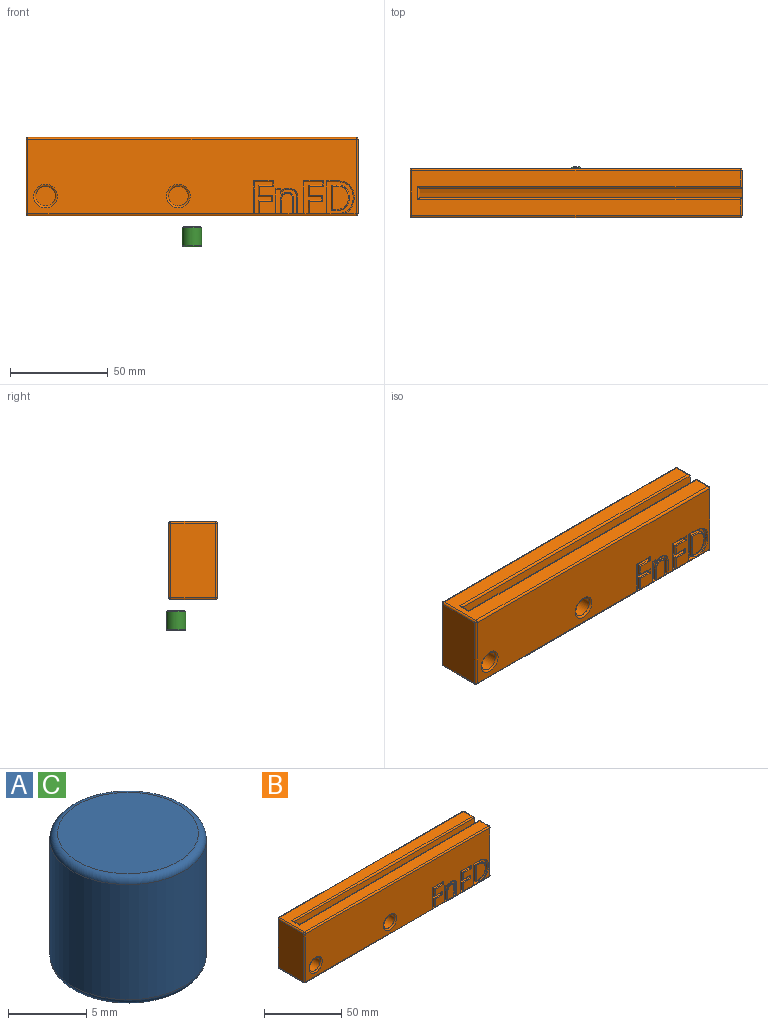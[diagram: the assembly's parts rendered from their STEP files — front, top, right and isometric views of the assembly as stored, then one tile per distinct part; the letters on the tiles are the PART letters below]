
ASSEMBLY  parts=3 mates=1
PART A: 5 faces, bbox 10.8x10.8x10 mm
  f0: cylinder r=5mm len=10mm, axis (0,0,-1), area 282.7mm2, adj f3,f4
  f1: plane 9x9mm, normal (0,0,1), area 63.6mm2, adj f4
  f2: plane 9x9mm, normal (0,0,-1), area 63.6mm2, adj f3
  f3: torus R=4.5mm, axis (0,0,1), area 23.8mm2, adj f0,f2
  f4: torus R=4.5mm, axis (0,0,1), area 23.8mm2, adj f0,f1
PART B: 249 faces, bbox 170.1x25.1x40.1 mm
  f0: plane 168x38.01mm, normal (0,-1,0), area 5632.2mm2, adj f21,f22,f24,f25,f27,f28,f165,f166
  f1: plane 10.36x5.51mm, normal (0,-1,0), area 54.3mm2, adj f27,f159,f160,f161,f162,f163,f164
  f2: plane 168x38.01mm, normal (0,1,0), area 5632.2mm2, adj f19,f20,f35,f36,f42,f43,f204,f205
  f3: plane 168x23mm, normal (0,0,1), area 2730.5mm2, adj f24,f33,f34,f38,f41,f42,f44,f46
  f4: plane 38x23mm, normal (-1,0,0), area 874mm2, adj f25,f26,f34,f35
  f5: plane 168x23mm, normal (0,0,-1), area 3864mm2, adj f26,f27,f36,f37
  f6: plane 38x23mm, normal (1,0,0), area 786.4mm2, adj f8,f9,f28,f33,f37,f43,f46
  f7: plane 10.36x5.51mm, normal (0,1,0), area 54.3mm2, adj f36,f213,f214,f215,f216,f217,f218
  f8: plane 165x36.07mm, normal (0,1,0.07), area 5964.7mm2, adj f6,f9,f10,f33,f38,f41
  f9: plane 165x36.07mm, normal (0,-1,0.07), area 5964.7mm2, adj f6,f8,f10,f41,f44,f46
  f10: plane 36x4.87mm, normal (1,0,0), area 87.6mm2, adj f8,f9,f41
  f11: cylinder r=5.05mm len=10.1mm, axis (0,-1,0), area 288.7mm2, adj f12,f21
  f12: plane 10.1x10.1mm, normal (0,-1,0), area 80.1mm2, adj f11
  f13: cylinder r=5.05mm len=10.1mm, axis (0,-1,0), area 288.7mm2, adj f14,f22
  f14: plane 10.1x10.1mm, normal (0,-1,0), area 80.1mm2, adj f13
  f15: cylinder r=5.05mm len=10.1mm, axis (0,1,0), area 288.7mm2, adj f16,f19
  f16: plane 10.1x10.1mm, normal (0,1,0), area 80.1mm2, adj f15
  f17: cylinder r=5.05mm len=10.1mm, axis (0,1,0), area 288.7mm2, adj f18,f20
  f18: plane 10.1x10.1mm, normal (0,1,0), area 80.1mm2, adj f17
  f19: torus R=6.05mm, axis (0,-1,0), area 53.4mm2, adj f2,f15
  f20: torus R=6.05mm, axis (0,-1,0), area 53.4mm2, adj f2,f17
  f21: torus R=6.05mm, axis (0,-1,0), area 53.4mm2, adj f0,f11
  f22: torus R=6.05mm, axis (0,-1,0), area 53.4mm2, adj f0,f13
  f23: sphere r=1mm, area 1.6mm2, adj f25,f26,f27
  f24: cylinder r=1mm len=168mm, axis (1,0,0), area 263.9mm2, adj f0,f3,f29,f30
  f25: cylinder r=1mm len=38mm, axis (0,0,1), area 59.7mm2, adj f0,f4,f23,f30
  f26: cylinder r=1mm len=23mm, axis (0,1,0), area 36.1mm2, adj f4,f5,f23,f31
  f27: cylinder r=1mm len=168mm, axis (-1,0,0), area 263.9mm2, adj f0,f1,f5,f23,f32,f112,f123,f130
  f28: cylinder r=1mm len=38mm, axis (0,0,-1), area 59.7mm2, adj f0,f6,f29,f32
  f29: sphere r=1mm, area 1.6mm2, adj f24,f28,f33
  f30: sphere r=1mm, area 1.6mm2, adj f24,f25,f34
  f31: sphere r=1mm, area 1.6mm2, adj f26,f35,f36
  f32: sphere r=1mm, area 1.6mm2, adj f27,f28,f37
  f33: cylinder r=1mm len=9.07mm, axis (0,1,0), area 13.7mm2, adj f3,f6,f8,f29,f38
  f34: cylinder r=1mm len=23mm, axis (0,-1,0), area 36.1mm2, adj f3,f4,f30,f39
  f35: cylinder r=1mm len=38mm, axis (0,0,-1), area 59.7mm2, adj f2,f4,f31,f39
  f36: cylinder r=1mm len=168mm, axis (1,0,0), area 263.9mm2, adj f2,f5,f7,f31,f40,f56,f59,f83
  f37: cylinder r=1mm len=23mm, axis (0,-1,0), area 36.1mm2, adj f5,f6,f32,f40
  f38: cylinder r=1mm len=166mm, axis (-1,0,0), area 248mm2, adj f3,f8,f33,f41
  f39: sphere r=1mm, area 1mm2, adj f34,f35,f42
  f40: sphere r=1mm, area 1mm2, adj f36,f37,f43
  f41: cylinder r=1mm len=6.87mm, axis (0,1,0), area 8.8mm2, adj f3,f8,f9,f10,f38,f44
  f42: cylinder r=1mm len=168mm, axis (-1,0,0), area 263.9mm2, adj f2,f3,f39,f45
  f43: cylinder r=1mm len=38mm, axis (0,0,1), area 59.7mm2, adj f2,f6,f40,f45
  f44: cylinder r=1mm len=166mm, axis (-1,0,0), area 248mm2, adj f3,f9,f41,f46
  f45: sphere r=1mm, area 1.6mm2, adj f42,f43,f46
  f46: cylinder r=1mm len=9.07mm, axis (0,1,0), area 13.7mm2, adj f3,f6,f9,f44,f45
  f47: plane 6.96x1.5mm, normal (1,0,0), area 10.4mm2, adj f48,f56,f57,f247
  f48: plane 6.75x1.5mm, normal (0,0,1), area 10.1mm2, adj f47,f49,f57,f248
  f49: plane 1.68x1.5mm, normal (1,0,0), area 2.5mm2, adj f48,f50,f57,f246
  f50: plane 6.75x1.5mm, normal (0,0,-1), area 10.1mm2, adj f49,f51,f57,f245
  f51: plane 5.96x1.5mm, normal (1,0,0), area 8.9mm2, adj f50,f52,f57,f244
  f52: plane 7.19x1.5mm, normal (0,0,1), area 10.8mm2, adj f51,f53,f57,f243
  f53: plane 1.68x1.5mm, normal (1,0,0), area 2.5mm2, adj f52,f54,f57,f242
  f54: plane 9.08x1.5mm, normal (0,0,-1), area 13.6mm2, adj f53,f55,f57,f241
  f55: plane 16.29x1.5mm, normal (-1,0,0), area 24.4mm2, adj f54,f56,f57,f240
  f56: plane 2.89x2mm, normal (0,0,1), area 3.9mm2, adj f36,f47,f55,f57,f240,f247
  f57: plane 16.29x9.08mm, normal (0,1,0), area 54.3mm2, adj f47,f48,f49,f50,f51,f52,f53,f54
  f58: plane 16.29x1.5mm, normal (-1,0,0), area 24.4mm2, adj f59,f71,f72,f228
  f59: plane 8.74x2.12mm, normal (0,0,1), area 9.8mm2, adj f36,f58,f60,f72,f227,f228
  f60: extruded ~6.3x2.13mm, area 10.2mm2, adj f59,f61,f72,f227
  f61: extruded ~6.17x2.19mm, area 10.1mm2, adj f60,f62,f72,f229
  f62: extruded ~5.88x2.11mm, area 9.6mm2, adj f61,f63,f72,f231
  f63: extruded ~5.9x2.11mm, area 9.7mm2, adj f62,f71,f72,f232
  f64: extruded ~4.93x1.71mm, area 8mm2, adj f65,f70,f72,f237
  f65: extruded ~5.09x1.67mm, area 8.2mm2, adj f64,f66,f72,f235
  f66: plane 2.31x1.5mm, normal (0,0,-1), area 3.5mm2, adj f65,f67,f72,f233
  f67: plane 13.01x1.5mm, normal (1,0,0), area 19.5mm2, adj f66,f68,f72,f234
  f68: plane 2.75x1.5mm, normal (0,0,1), area 4.1mm2, adj f67,f69,f72,f236
  f69: extruded ~4.75x1.61mm, area 7.7mm2, adj f68,f70,f72,f238
  f70: extruded ~4.8x1.6mm, area 7.8mm2, adj f64,f69,f72,f239
  f71: plane 4.99x1.5mm, normal (0,0,-1), area 7.5mm2, adj f58,f63,f72,f230
  f72: plane 16.29x13mm, normal (0,1,0), area 83.9mm2, adj f58,f59,f60,f61,f62,f63,f64,f65
  f73: plane 12.01x8.1mm, normal (0,1,0), area 85.3mm2, adj f233,f234,f235,f236,f237,f238,f239
  f74: plane 7.96x1.5mm, normal (1,0,0), area 11.9mm2, adj f75,f90,f91,f225
  f75: extruded ~3.41x1.5mm, area 5.5mm2, adj f74,f76,f91,f226
  f76: extruded ~3.32x1.5mm, area 5.4mm2, adj f75,f77,f91,f224
  f77: extruded ~2.28x1.5mm, area 3.5mm2, adj f76,f78,f91,f223
  f78: extruded ~1.6x1.5mm, area 3.2mm2, adj f77,f79,f91,f222
  f79: plane 1.71x0.1mm, normal (0,0,-1), area 0.1mm2, adj f78,f80,f91,f221,f222
  f80: plane 1.67x1.5mm, normal (0.98,0,-0.18), area 2.5mm2, adj f79,f81,f91,f221
  f81: plane 1.5x1.5mm, normal (0,0,-1), area 2.3mm2, adj f80,f82,f91,f220
  f82: plane 12.21x1.5mm, normal (-1,0,0), area 18.3mm2, adj f81,f83,f91,f219
  f83: plane 2.85x2mm, normal (0,0,1), area 3.8mm2, adj f36,f82,f84,f91,f213,f219
  f84: plane 6.41x1.5mm, normal (1,0,0), area 9.6mm2, adj f83,f85,f91,f213
  f85: extruded ~3.42x1.5mm, area 5.4mm2, adj f84,f86,f91,f214
  f86: extruded ~2.81x1.5mm, area 4.6mm2, adj f85,f87,f91,f215
  f87: extruded ~2.13x1.5mm, area 3.5mm2, adj f86,f88,f91,f217
  f88: extruded ~2.23x1.5mm, area 3.6mm2, adj f87,f89,f91,f218
  f89: plane 7.9x1.5mm, normal (-1,0,0), area 11.8mm2, adj f88,f90,f91,f216
  f90: plane 2.85x2mm, normal (0,0,1), area 3.8mm2, adj f36,f74,f89,f91,f216,f225
  f91: plane 12.43x10.21mm, normal (0,1,0), area 54mm2, adj f74,f75,f76,f77,f78,f79,f80,f81
  f92: plane 6.96x1.5mm, normal (1,0,0), area 10.4mm2, adj f93,f101,f102,f211
  f93: plane 6.75x1.5mm, normal (0,0,1), area 10.1mm2, adj f92,f94,f102,f212
  f94: plane 1.68x1.5mm, normal (1,0,0), area 2.5mm2, adj f93,f95,f102,f210
  f95: plane 6.75x1.5mm, normal (0,0,-1), area 10.1mm2, adj f94,f96,f102,f209
  f96: plane 5.96x1.5mm, normal (1,0,0), area 8.9mm2, adj f95,f97,f102,f208
  f97: plane 7.19x1.5mm, normal (0,0,1), area 10.8mm2, adj f96,f98,f102,f207
  f98: plane 1.68x1.5mm, normal (1,0,0), area 2.5mm2, adj f97,f99,f102,f206
  f99: plane 9.08x1.5mm, normal (0,0,-1), area 13.6mm2, adj f98,f100,f102,f205
  f100: plane 16.29x1.5mm, normal (-1,0,0), area 24.4mm2, adj f99,f101,f102,f204
  f101: plane 2.89x2mm, normal (0,0,1), area 3.9mm2, adj f36,f92,f100,f102,f204,f211
  f102: plane 16.29x9.08mm, normal (0,1,0), area 54.3mm2, adj f92,f93,f94,f95,f96,f97,f98,f99
  f103: plane 6.96x1.5mm, normal (-1,0,0), area 10.4mm2, adj f104,f112,f113,f172
  f104: plane 6.75x1.5mm, normal (0,0,1), area 10.1mm2, adj f103,f105,f113,f173
  f105: plane 1.68x1.5mm, normal (-1,0,0), area 2.5mm2, adj f104,f106,f113,f171
  f106: plane 6.75x1.5mm, normal (0,0,-1), area 10.1mm2, adj f105,f107,f113,f170
  f107: plane 5.96x1.5mm, normal (-1,0,0), area 8.9mm2, adj f106,f108,f113,f169
  f108: plane 7.19x1.5mm, normal (0,0,1), area 10.8mm2, adj f107,f109,f113,f168
  f109: plane 1.68x1.5mm, normal (-1,0,0), area 2.5mm2, adj f108,f110,f113,f167
  f110: plane 9.08x1.5mm, normal (0,0,-1), area 13.6mm2, adj f109,f111,f113,f166
  f111: plane 16.29x1.5mm, normal (1,0,0), area 24.4mm2, adj f110,f112,f113,f165
  f112: plane 2.89x2mm, normal (0,0,1), area 3.9mm2, adj f27,f103,f111,f113,f165,f172
  f113: plane 16.29x9.08mm, normal (0,-1,0), area 54.3mm2, adj f103,f104,f105,f106,f107,f108,f109,f110
  f114: plane 7.96x1.5mm, normal (-1,0,0), area 11.9mm2, adj f115,f130,f131,f180
  f115: extruded ~3.41x1.5mm, area 5.5mm2, adj f114,f116,f131,f181
  f116: extruded ~3.32x1.5mm, area 5.4mm2, adj f115,f117,f131,f179
  f117: extruded ~2.28x1.5mm, area 3.5mm2, adj f116,f118,f131,f178
  f118: extruded ~1.6x1.5mm, area 3.2mm2, adj f117,f119,f131,f177
  f119: plane 1.71x0.1mm, normal (0,0,-1), area 0.1mm2, adj f118,f120,f131,f176,f177
  f120: plane 1.67x1.5mm, normal (-0.98,0,-0.18), area 2.5mm2, adj f119,f121,f131,f176
  f121: plane 1.5x1.5mm, normal (0,0,-1), area 2.3mm2, adj f120,f122,f131,f175
  f122: plane 12.21x1.5mm, normal (1,0,0), area 18.3mm2, adj f121,f123,f131,f174
  f123: plane 2.85x2mm, normal (0,0,1), area 3.8mm2, adj f27,f122,f124,f131,f164,f174
  f124: plane 6.41x1.5mm, normal (-1,0,0), area 9.6mm2, adj f123,f125,f131,f164
  f125: extruded ~3.42x1.5mm, area 5.4mm2, adj f124,f126,f131,f163
  f126: extruded ~2.81x1.5mm, area 4.6mm2, adj f125,f127,f131,f162
  f127: extruded ~2.13x1.5mm, area 3.5mm2, adj f126,f128,f131,f161
  f128: extruded ~2.23x1.5mm, area 3.6mm2, adj f127,f129,f131,f160
  f129: plane 7.9x1.5mm, normal (1,0,0), area 11.8mm2, adj f128,f130,f131,f159
  f130: plane 2.85x2mm, normal (0,0,1), area 3.8mm2, adj f27,f114,f129,f131,f159,f180
  f131: plane 12.43x10.21mm, normal (0,-1,0), area 54mm2, adj f114,f115,f116,f117,f118,f119,f120,f121
  f132: plane 6.96x1.5mm, normal (-1,0,0), area 10.4mm2, adj f133,f141,f142,f182
  f133: plane 6.75x1.5mm, normal (0,0,1), area 10.1mm2, adj f132,f134,f142,f183
  f134: plane 1.68x1.5mm, normal (-1,0,0), area 2.5mm2, adj f133,f135,f142,f184
  f135: plane 6.75x1.5mm, normal (0,0,-1), area 10.1mm2, adj f134,f136,f142,f185
  f136: plane 5.96x1.5mm, normal (-1,0,0), area 8.9mm2, adj f135,f137,f142,f186
  f137: plane 7.19x1.5mm, normal (0,0,1), area 10.8mm2, adj f136,f138,f142,f187
  f138: plane 1.68x1.5mm, normal (-1,0,0), area 2.5mm2, adj f137,f139,f142,f188
  f139: plane 9.08x1.5mm, normal (0,0,-1), area 13.6mm2, adj f138,f140,f142,f189
  f140: plane 16.29x1.5mm, normal (1,0,0), area 24.4mm2, adj f139,f141,f142,f190
  f141: plane 2.89x2mm, normal (0,0,1), area 3.9mm2, adj f27,f132,f140,f142,f182,f190
  f142: plane 16.29x9.08mm, normal (0,-1,0), area 54.3mm2, adj f132,f133,f134,f135,f136,f137,f138,f139
  f143: plane 16.29x1.5mm, normal (1,0,0), area 24.4mm2, adj f144,f156,f157,f192
  f144: plane 8.74x2.12mm, normal (0,0,1), area 9.8mm2, adj f27,f143,f145,f157,f191,f192
  f145: extruded ~6.3x2.13mm, area 10.2mm2, adj f144,f146,f157,f191
  f146: extruded ~6.17x2.19mm, area 10.1mm2, adj f145,f147,f157,f193
  f147: extruded ~5.88x2.11mm, area 9.6mm2, adj f146,f148,f157,f195
  f148: extruded ~5.9x2.11mm, area 9.7mm2, adj f147,f156,f157,f196
  f149: extruded ~4.93x1.71mm, area 8mm2, adj f150,f155,f157,f202
  f150: extruded ~5.09x1.67mm, area 8.2mm2, adj f149,f151,f157,f203
  f151: plane 2.31x1.5mm, normal (0,0,-1), area 3.5mm2, adj f150,f152,f157,f201
  f152: plane 13.01x1.5mm, normal (-1,0,0), area 19.5mm2, adj f151,f153,f157,f199
  f153: plane 2.75x1.5mm, normal (0,0,1), area 4.1mm2, adj f152,f154,f157,f197
  f154: extruded ~4.75x1.61mm, area 7.7mm2, adj f153,f155,f157,f198
  f155: extruded ~4.8x1.6mm, area 7.8mm2, adj f149,f154,f157,f200
  f156: plane 4.99x1.5mm, normal (0,0,-1), area 7.5mm2, adj f143,f148,f157,f194
  f157: plane 16.29x13mm, normal (0,-1,0), area 83.9mm2, adj f143,f144,f145,f146,f147,f148,f149,f150
  f158: plane 12.01x8.1mm, normal (0,-1,0), area 85.3mm2, adj f197,f198,f199,f200,f201,f202,f203
  f159: cylinder r=0.5mm len=7.9mm, axis (0,0,1), area 6.2mm2, adj f1,f129,f130,f160
  f160: bspline ~3.42x1.34mm, area 1.8mm2, adj f1,f128,f159,f161
  f161: bspline ~3.1x1.34mm, area 1.7mm2, adj f1,f127,f160,f162
  f162: bspline ~3.37x1.72mm, area 2.3mm2, adj f1,f126,f161,f163
  f163: bspline ~5.58x1.78mm, area 2.7mm2, adj f1,f125,f162,f164
  f164: cylinder r=0.5mm len=6.41mm, axis (0,0,-1), area 5mm2, adj f1,f123,f124,f163
  f165: cylinder r=0.5mm len=16.79mm, axis (0,0,1), area 13mm2, adj f0,f111,f112,f166
  f166: cylinder r=0.5mm len=10.08mm, axis (1,0,0), area 7.5mm2, adj f0,f110,f165,f167
  f167: cylinder r=0.5mm len=2.68mm, axis (0,0,-1), area 1.7mm2, adj f0,f109,f166,f168
  f168: cylinder r=0.5mm len=7.69mm, axis (-1,0,0), area 5.6mm2, adj f0,f108,f167,f169
  f169: cylinder r=0.5mm len=5.96mm, axis (0,0,-1), area 4.3mm2, adj f0,f107,f168,f170
  f170: cylinder r=0.5mm len=7.25mm, axis (1,0,0), area 5.3mm2, adj f0,f106,f169,f171
  f171: cylinder r=0.5mm len=2.68mm, axis (0,0,-1), area 1.7mm2, adj f0,f105,f170,f173
  f172: cylinder r=0.5mm len=6.96mm, axis (0,0,-1), area 5.3mm2, adj f0,f103,f112,f173
  f173: cylinder r=0.5mm len=7.25mm, axis (-1,0,0), area 5.3mm2, adj f0,f104,f171,f172
  f174: cylinder r=0.5mm len=12.71mm, axis (0,0,1), area 9.8mm2, adj f0,f122,f123,f175
  f175: cylinder r=0.5mm len=2.42mm, axis (1,0,0), area 1.5mm2, adj f0,f121,f174,f176
  f176: cylinder r=0.5mm len=2.18mm, axis (0.18,0,-0.98), area 1.2mm2, adj f0,f119,f120,f175,f177
  f177: bspline ~2.45x2.41mm, area 1.5mm2, adj f0,f118,f119,f176,f178
  f178: bspline ~3.38x1.2mm, area 1.9mm2, adj f0,f117,f177,f179
  f179: bspline ~5.49x2.03mm, area 2.9mm2, adj f0,f116,f178,f181
  f180: cylinder r=0.5mm len=7.96mm, axis (0,0,-1), area 6.3mm2, adj f0,f114,f130,f181
  f181: bspline ~5.52x2.09mm, area 3mm2, adj f0,f115,f179,f180
  f182: cylinder r=0.5mm len=6.96mm, axis (0,0,-1), area 5.3mm2, adj f0,f132,f141,f183
  f183: cylinder r=0.5mm len=7.25mm, axis (-1,0,0), area 5.3mm2, adj f0,f133,f182,f184
  f184: cylinder r=0.5mm len=2.68mm, axis (0,0,-1), area 1.7mm2, adj f0,f134,f183,f185
  f185: cylinder r=0.5mm len=7.25mm, axis (1,0,0), area 5.3mm2, adj f0,f135,f184,f186
  f186: cylinder r=0.5mm len=5.96mm, axis (0,0,-1), area 4.3mm2, adj f0,f136,f185,f187
  f187: cylinder r=0.5mm len=7.69mm, axis (-1,0,0), area 5.6mm2, adj f0,f137,f186,f188
  f188: cylinder r=0.5mm len=2.68mm, axis (0,0,-1), area 1.7mm2, adj f0,f138,f187,f189
  f189: cylinder r=0.5mm len=10.08mm, axis (1,0,0), area 7.5mm2, adj f0,f139,f188,f190
  f190: cylinder r=0.5mm len=16.79mm, axis (0,0,1), area 13mm2, adj f0,f140,f141,f189
  f191: bspline ~8.07x3.78mm, area 4.1mm2, adj f0,f144,f145,f193
  f192: cylinder r=0.5mm len=16.79mm, axis (0,0,1), area 13mm2, adj f0,f143,f144,f194
  f193: bspline ~8.01x3.58mm, area 5.4mm2, adj f0,f146,f191,f195
  f194: cylinder r=0.5mm len=5.49mm, axis (1,0,0), area 4.1mm2, adj f0,f156,f192,f196
  f195: bspline ~9.47x3.45mm, area 5.2mm2, adj f0,f147,f193,f196
  f196: bspline ~8.87x2.81mm, area 5.2mm2, adj f0,f148,f194,f195
  f197: cylinder r=0.5mm len=2.75mm, axis (-1,0,0), area 2mm2, adj f153,f158,f198,f199
  f198: bspline ~7.33x2.64mm, area 3.9mm2, adj f154,f158,f197,f200
  f199: cylinder r=0.5mm len=13.01mm, axis (0,0,-1), area 9.8mm2, adj f152,f158,f197,f201
  f200: bspline ~7.45x2.64mm, area 4mm2, adj f155,f158,f198,f202
  f201: cylinder r=0.5mm len=2.31mm, axis (1,0,0), area 1.6mm2, adj f151,f158,f199,f203
  f202: bspline ~6.11x2.76mm, area 4.1mm2, adj f149,f158,f200,f203
  f203: bspline ~7.95x2.76mm, area 4.2mm2, adj f150,f158,f201,f202
  f204: cylinder r=0.5mm len=16.79mm, axis (0,0,-1), area 13mm2, adj f2,f100,f101,f205
  f205: cylinder r=0.5mm len=10.08mm, axis (1,0,0), area 7.5mm2, adj f2,f99,f204,f206
  f206: cylinder r=0.5mm len=2.68mm, axis (0,0,1), area 1.7mm2, adj f2,f98,f205,f207
  f207: cylinder r=0.5mm len=7.69mm, axis (-1,0,0), area 5.6mm2, adj f2,f97,f206,f208
  f208: cylinder r=0.5mm len=5.96mm, axis (0,0,1), area 4.3mm2, adj f2,f96,f207,f209
  f209: cylinder r=0.5mm len=7.25mm, axis (1,0,0), area 5.3mm2, adj f2,f95,f208,f210
  f210: cylinder r=0.5mm len=2.68mm, axis (0,0,1), area 1.7mm2, adj f2,f94,f209,f212
  f211: cylinder r=0.5mm len=6.96mm, axis (0,0,1), area 5.3mm2, adj f2,f92,f101,f212
  f212: cylinder r=0.5mm len=7.25mm, axis (-1,0,0), area 5.3mm2, adj f2,f93,f210,f211
  f213: cylinder r=0.5mm len=6.41mm, axis (0,0,1), area 5mm2, adj f7,f83,f84,f214
  f214: bspline ~5.58x1.78mm, area 2.7mm2, adj f7,f85,f213,f215
  f215: bspline ~4.08x1.72mm, area 2.3mm2, adj f7,f86,f214,f217
  f216: cylinder r=0.5mm len=7.9mm, axis (0,0,-1), area 6.2mm2, adj f7,f89,f90,f218
  f217: bspline ~2.93x1.14mm, area 1.7mm2, adj f7,f87,f215,f218
  f218: bspline ~3.42x1.34mm, area 1.8mm2, adj f7,f88,f216,f217
  f219: cylinder r=0.5mm len=12.71mm, axis (0,0,-1), area 9.8mm2, adj f2,f82,f83,f220
  f220: cylinder r=0.5mm len=2.42mm, axis (1,0,0), area 1.5mm2, adj f2,f81,f219,f221
  f221: cylinder r=0.5mm len=2.18mm, axis (0.18,0,0.98), area 1.2mm2, adj f2,f79,f80,f220,f222
  f222: bspline ~2.82x2.59mm, area 1.5mm2, adj f2,f78,f79,f221,f223
  f223: bspline ~3.07x1.05mm, area 1.9mm2, adj f2,f77,f222,f224
  f224: bspline ~5.49x2.03mm, area 2.9mm2, adj f2,f76,f223,f226
  f225: cylinder r=0.5mm len=7.96mm, axis (0,0,1), area 6.3mm2, adj f2,f74,f90,f226
  f226: bspline ~5.52x2.09mm, area 3mm2, adj f2,f75,f224,f225
  f227: bspline ~8.07x3.78mm, area 4.1mm2, adj f2,f59,f60,f229
  f228: cylinder r=0.5mm len=16.79mm, axis (0,0,-1), area 13mm2, adj f2,f58,f59,f230
  f229: bspline ~9.87x3.58mm, area 5.4mm2, adj f2,f61,f227,f231
  f230: cylinder r=0.5mm len=5.49mm, axis (1,0,0), area 4.1mm2, adj f2,f71,f228,f232
  f231: bspline ~9.47x3.45mm, area 5.2mm2, adj f2,f62,f229,f232
  f232: bspline ~9.51x3.45mm, area 5.2mm2, adj f2,f63,f230,f231
  f233: cylinder r=0.5mm len=2.31mm, axis (1,0,0), area 1.6mm2, adj f66,f73,f234,f235
  f234: cylinder r=0.5mm len=13.01mm, axis (0,0,1), area 9.8mm2, adj f67,f73,f233,f236
  f235: bspline ~7.95x2.76mm, area 4.2mm2, adj f65,f73,f233,f237
  f236: cylinder r=0.5mm len=2.75mm, axis (-1,0,0), area 2mm2, adj f68,f73,f234,f238
  f237: bspline ~7.07x2.23mm, area 4.1mm2, adj f64,f73,f235,f239
  f238: bspline ~7.33x2.64mm, area 3.9mm2, adj f69,f73,f236,f239
  f239: bspline ~7.45x2.64mm, area 4mm2, adj f70,f73,f237,f238
  f240: cylinder r=0.5mm len=16.79mm, axis (0,0,-1), area 13mm2, adj f2,f55,f56,f241
  f241: cylinder r=0.5mm len=10.08mm, axis (1,0,0), area 7.5mm2, adj f2,f54,f240,f242
  f242: cylinder r=0.5mm len=2.68mm, axis (0,0,1), area 1.7mm2, adj f2,f53,f241,f243
  f243: cylinder r=0.5mm len=7.69mm, axis (-1,0,0), area 5.6mm2, adj f2,f52,f242,f244
  f244: cylinder r=0.5mm len=5.96mm, axis (0,0,1), area 4.3mm2, adj f2,f51,f243,f245
  f245: cylinder r=0.5mm len=7.25mm, axis (1,0,0), area 5.3mm2, adj f2,f50,f244,f246
  f246: cylinder r=0.5mm len=2.68mm, axis (0,0,1), area 1.7mm2, adj f2,f49,f245,f248
  f247: cylinder r=0.5mm len=6.96mm, axis (0,0,1), area 5.3mm2, adj f2,f47,f56,f248
  f248: cylinder r=0.5mm len=7.25mm, axis (-1,0,0), area 5.3mm2, adj f2,f48,f246,f247
PART C: same geometry as A
PLACE A rot(axis=(-1,0,0),90deg) t=(-6.99,-6.31,25.8)mm
PLACE B t=(-6.95,3.79,33.27)mm
PLACE C at identity
MATE fastened A.f0 <-> B.f11  axis (0,-1,0) through (-6.99,-6.31,25.8)mm
